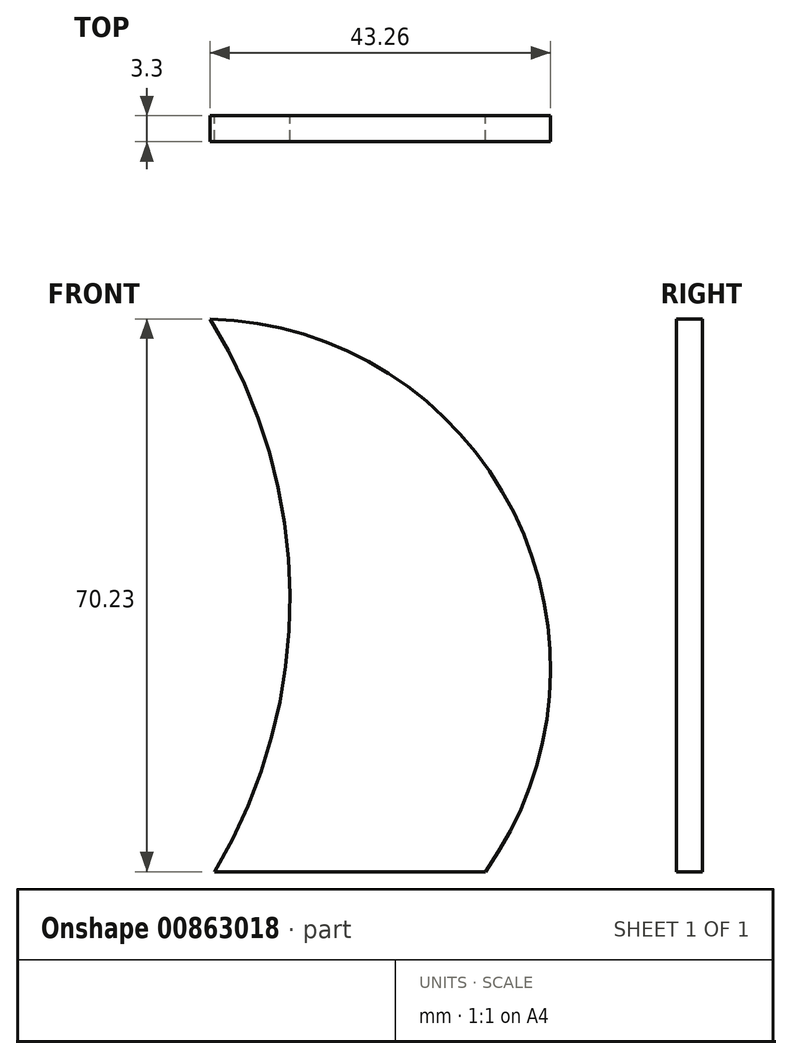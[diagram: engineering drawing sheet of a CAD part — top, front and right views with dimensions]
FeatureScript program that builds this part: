
annotation { "Feature Type Name" : "Feature", "Feature Type Description" : "" }
export const myFeature = defineFeature(function(context is Context, id is Id, definition is map)
    precondition{}
    {
        {
            var Q0;
            Q0=qCreatedBy(makeId("Front.planeOp"),FACE);
            var sketch = newSketch(context, id + "F0", { "sketchPlane" : qUnion([Q0])});
            skArc(sketch, "E0", {"start": v(-19.71, -35.26) * mm, "mid": v(-10.11, -0.06) * mm, "end": v(-20.3, 34.97) * mm});
            skLineSegment(sketch, "E1", {"start": v(-19.71, -35.26) * mm, "end": v(14.7, -35.26) * mm});
            skArc(sketch, "E2", {"start": v(14.7, -35.26) * mm, "mid": v(18.3, 10.37) * mm, "end": v(-20.3, 34.97) * mm});
            skSolve(sketch);
        }
        {
            var Q0;
            Q0=makeQuery(id+"F0.imprint","IMPRINT",FACE,{"disambiguationData":[TD([[makeQuery(id+"F0.imprint","IMPRINT",EDGE,{"derivedFrom":sQuery(id+"F0.wireOp",EDGE,"E0")}),-1.0]])]});
            extrude(context, id + "F1", {"entities" : qUnion([Q0]), "depth" : 3.3 * mm, "offsetDistance" : 25.4 * mm});
        }
    });
